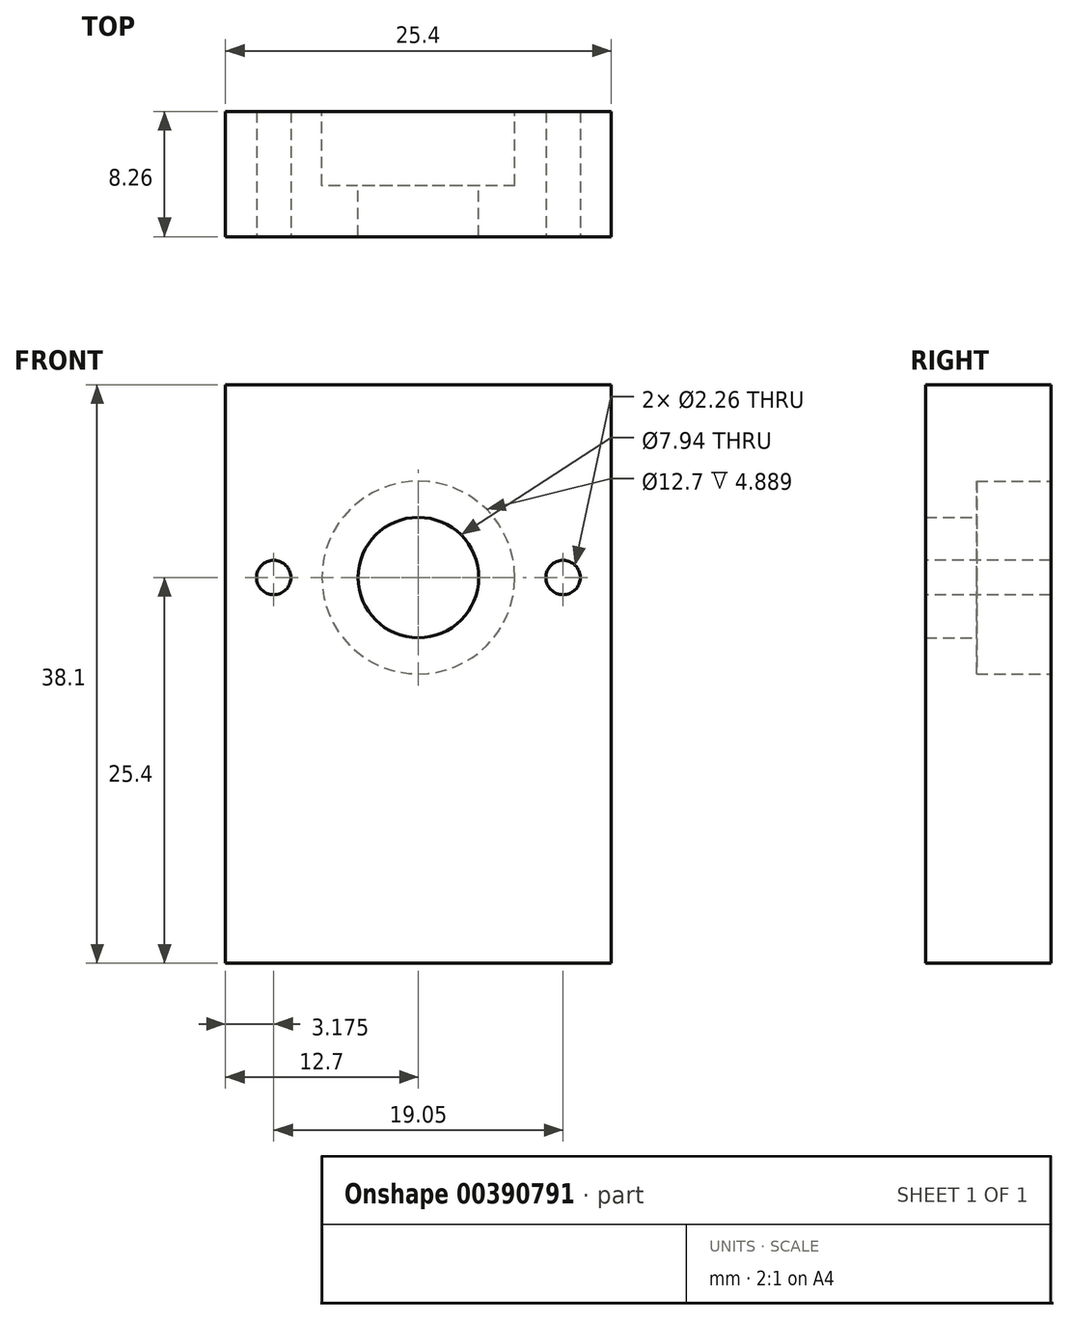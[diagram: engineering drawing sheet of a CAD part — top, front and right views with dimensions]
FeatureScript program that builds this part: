
annotation { "Feature Type Name" : "Feature", "Feature Type Description" : "" }
export const myFeature = defineFeature(function(context is Context, id is Id, definition is map)
    precondition{}
    {
        {
            var Q0;
            Q0=qCreatedBy(makeId("Front.planeOp"),FACE);
            var sketch = newSketch(context, id + "F0", { "sketchPlane" : qUnion([Q0]), "asVersion" : FeatureScriptVersionNumber.V593_MASTER_MODEL_DOC});
            skLineSegment(sketch, "E0.bottom", {"start": v(0, 0) * mm, "end": v(25.4, 0) * mm});
            skLineSegment(sketch, "E0.top", {"start": v(0, 38.1) * mm, "end": v(25.4, 38.1) * mm});
            skLineSegment(sketch, "E0.left", {"start": v(0, 0) * mm, "end": v(0, 38.1) * mm});
            skLineSegment(sketch, "E0.right", {"start": v(25.4, 0) * mm, "end": v(25.4, 38.1) * mm});
            skCircle(sketch, "E1", {"center": v(12.7, 25.4) * mm, "radius": 6.35 * mm});
            skPoint(sketch, "E1.centerSnap0", {"position": v(12.7, 38.1) * mm});
            skCircle(sketch, "E2", {"center": v(12.7, 25.4) * mm, "radius": 3.97 * mm});
            skPoint(sketch, "E3", {"position": v(22.23, 25.4) * mm});
            skPoint(sketch, "E4", {"position": v(3.17, 25.4) * mm});
            skSolve(sketch);
        }
        {
            var Q0;
            Q0=makeQuery(id+"F0.imprint","IMPRINT",FACE,{"disambiguationData":[TD([[makeQuery(id+"F0.imprint","IMPRINT",EDGE,{"derivedFrom":sQuery(id+"F0.wireOp",EDGE,"E0.bottom")}),1.0]])]});
            var Q1;
            Q1=makeQuery(id+"F0.imprint","IMPRINT",FACE,{"disambiguationData":[TD([[makeQuery(id+"F0.imprint","IMPRINT",EDGE,{"derivedFrom":sQuery(id+"F0.wireOp",EDGE,"E1")}),1.0]])]});
            extrude(context, id + "F1", {"entities" : qUnion([Q0, Q1]), "depth" : 8.25 * mm, "offsetDistance" : 25.4 * mm});
        }
        {
            var Q0;
            Q0=makeQuery(id+"F0.imprint","IMPRINT",FACE,{"disambiguationData":[TD([[makeQuery(id+"F0.imprint","IMPRINT",EDGE,{"derivedFrom":sQuery(id+"F0.wireOp",EDGE,"E1")}),1.0]])]});
            extrude(context, id + "F2", {"entities" : qUnion([Q0]), "operationType" : NewBodyOperationType.REMOVE, "depth" : 4.89 * mm, "offsetDistance" : 25.4 * mm});
        }
        {
            var Q0;
            Q0=sQuery(id+"F0.wireOp",VERTEX,"E3");
            var Q1;
            Q1=sQuery(id+"F0.wireOp",VERTEX,"E4");
            var Q2;
            Q2=makeQuery(id+"F1.opExtrude","SWEPT_BODY",BODY,{"disambiguationData":[OSD([sQuery(id+"F0.wireOp",EDGE,"E0.bottom"),sQuery(id+"F0.wireOp",EDGE,"E0.top"),sQuery(id+"F0.wireOp",EDGE,"E0.left"),sQuery(id+"F0.wireOp",EDGE,"E0.right"),sQuery(id+"F0.wireOp",EDGE,"E2")])]});
            hole(context, id + "F3", {"style" : HoleStyle.SIMPLE, "endStyle" : HoleEndStyle.THROUGH, "oppositeDirection" : true, "standardTappedOrClearance" : lookupTablePath({ "standard" : "ANSI", "engagement" : "75%", "pitch" : "40 tpi", "size" : "#4", "type" : "Tapped" }), "standardBlindInLast" : lookupTablePath({ "standard" : "ANSI", "engagement" : "75%", "pitch" : "40 tpi", "size" : "#4", "type" : "Tapped" }), "holeDiameter" : 2.26 * mm, "showTappedDepth" : true, "isTappedThrough" : true, "tappedDepth" : 4.44 * mm, "tapClearance" : 3, "locations" : qUnion([Q0, Q1]), "scope" : qUnion([Q2]), "majorDiameter" : 2.84 * mm});
        }
    });
